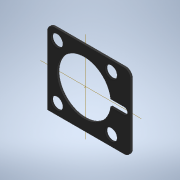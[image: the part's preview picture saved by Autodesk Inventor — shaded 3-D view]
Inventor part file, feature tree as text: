
AUTODESK INVENTOR PART (.ipt)
format: ipt  version: 2021.1 (Build 251245000, 245)  size: 146,944 bytes
history: native  units: in
note: dims shown in document units (in); Inventor stores cm internally (conversion verified against a paired STEP export)
features: extrude x1, sketch x1
ambient origin geometry x8: Origin, YZ Plane, XZ Plane, XY Plane, X Axis, Y Axis, Z Axis, Center Point
bodies: Solid1 (feature_tree)
feature tree (2):
  extrude  "Extrusion1"  Depth=4.5in
  sketch  "Sketch1"  dims[d0=5.0in d1=4.5in d2=2.2in d3=3.2in d4=4.6in d5=0.4in d6=45.0deg d7=0.7in d8=1.5748in d10=360.0deg d12=0.4in d13=0.4in d14=2.4in d15=0.1in d16=0.0in]
